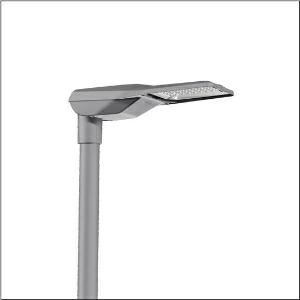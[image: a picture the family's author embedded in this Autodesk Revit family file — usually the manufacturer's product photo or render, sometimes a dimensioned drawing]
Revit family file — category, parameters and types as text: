
# Revit family: streetlight_sl_21_iq_mini___st1_0a_5xe2d31g08gb_f91a
name_source: partatom
category: Lighting Fixtures
units: mm (PartAtom-declared; Revit-internal decimal feet)

## family parameters
Cut with Voids When Loaded = No
Host = Face
Light Source = No
Part Type = Normal
Room Calculation Point = No
Round Connector Dimension = Use Diameter
Shared = No

## types (1)
- --- (1 x LED, 5680 lm, 37.1 W, 3000K)
    Apparent Load = 37 VA
    CIE Flux Codes = 37 72 97 100 100
    Color Rendering = 70
    Color Temperature = 3000K
    Default Elevation = 1800 mm
    Description = Streetlight SL 21 iQ mini, mast luminaire, primary light control with lens, of PMMA, primary optical cover: cover, of toughened safety glass, transparent, light distribution: ST1.0a, light emission: direct distribution, primary light characteristic: asymmetric, installation type: post-top, side-entry, LED, High Power LED, rated luminous flux: 5.680lm, luminous efficacy: 153lm/W, light colour: 730, colour temperature: 3000K, control: Street-Remote, Auto-Match, Temp-Guard, Lumen-Switch, Night-Set, Smart-Wire, Light-Fading, Desk-Remote (wireless, voltage-free reading and setting of iQ features in the workshop via application-optimized NFC function/RFID function), optimised constant luminous flux control (CLO 2.0), presetting dimming linear, mains connection: 220..240V, AC, 50/60Hz, start of lifetime: 37W, end of service life: 39W, reduction: 18W, luminaire housing, of diecast aluminium, powder-coated, Siteco® metallic grey (DB 702S), corrosivity category C5 mid according to DIN EN ISO 12944, please order mast flange separately, inclination adjustable: 0°, 5°, 10°, 15°, sealing non-destructively replaceable, multi-level sealing system, length: 628mm, width: 235mm, height: 110mm, mast flange for spigot size: 42mm (side-entry): 5XC10008XM4, 60/48mm (side-entry/post-top): 5XC10108XM2, 76/60mm (side-entry/post-top): 5XC10108XM1, protection rating (complete): IP66, insulation class (complete): insulation class II (safety insulation), certification: CE, ENEC, ENEC+, VDE, impact resistance: IK09, permissible operating ambient temperature for outdoor applications: -40..+50°C, standard-compliant lighting for roads and squares, packaging unit: 1 piece

Light Distribution: ST1.0a
    Height = 110 mm
    Lamp = 1 x LED
    Lamp Light Flux = 5680 lm
    Lamp Power = 37.1 W
    Lamp count = 1
    Length = 625 mm
    Luminous efficacy = 153 lm/W
    Manufacturer = Siteco
    ModVariant = No
    Model = 5XE2D31G08GB
    Number of Poles = 1
    OnlyDefault = Yes
    Power Factor = 1
    Product Name = Streetlight SL 21 iQ mini | ST1.0a
    Product group = mast luminaire | pylon top
    ProductGroupID = 6100
    Protection Class = Protection class II
    Protection Degree = IP 66
    RLX_Detail_Level = 1
    RLX_Emergency_Light_Flux = 0 lm
    RLX_Emergency_Type = 0
    RLX_Emergency_Type_DB = No
    RlxData = <blob elided: 92297 chars, md5=9021072f>
    Socket = socket
    Standby Power = 0 W
    System Light Flux = 5680 lm
    System Power = 37 W
    Type Comments = factory setting: luminous flux: 100 % | dim-lin: 254 | 385 mA
    Type Image = l_1003519.jpg
    URL = http://relux.com
    VarID = @adj_122643
    Voltage = 0 V
    Weight = 0.00 kg
    Width = 234 mm

## geometry (parser evidence)
native form markers: Blend x4, Sweep x12
no freeform markers — native parametric forms only
